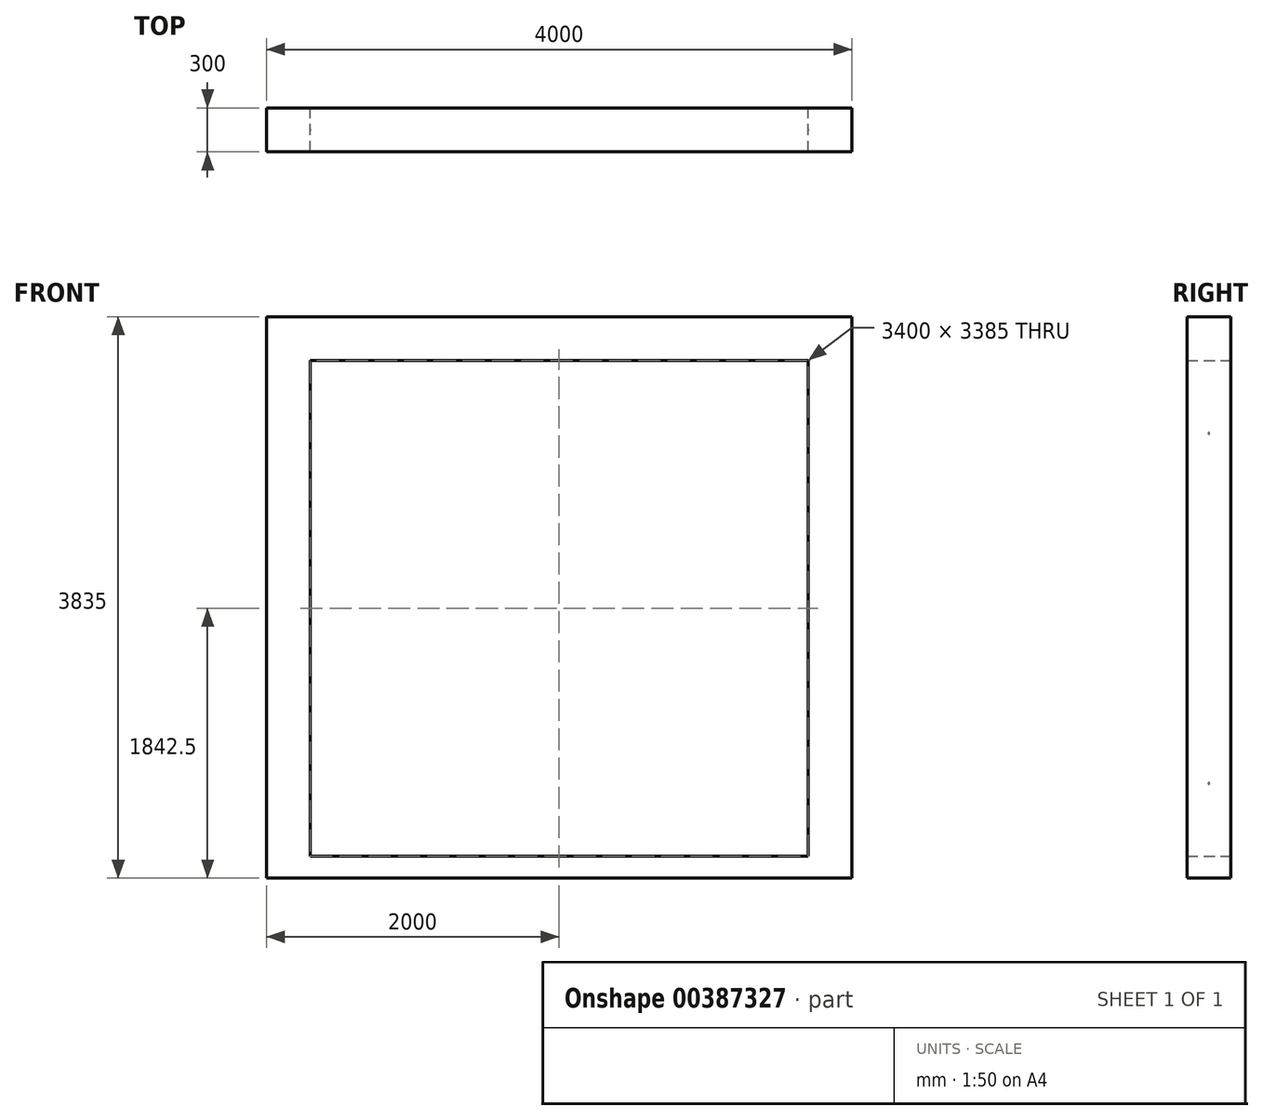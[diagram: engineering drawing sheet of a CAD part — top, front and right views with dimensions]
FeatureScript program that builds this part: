
annotation { "Feature Type Name" : "Feature", "Feature Type Description" : "" }
export const myFeature = defineFeature(function(context is Context, id is Id, definition is map)
    precondition{}
    {
        {
            var Q0;
            Q0=qCreatedBy(makeId("Front.planeOp"),FACE);
            var sketch = newSketch(context, id + "F0", { "sketchPlane" : qUnion([Q0])});
            skLineSegment(sketch, "E0.bottom", {"start": v(-3031.65, 3246.47) * mm, "end": v(368.35, 3246.47) * mm});
            skLineSegment(sketch, "E0.top", {"start": v(-3031.65, -138.53) * mm, "end": v(368.35, -138.53) * mm});
            skLineSegment(sketch, "E0.left", {"start": v(-3031.65, 3246.47) * mm, "end": v(-3031.65, -138.53) * mm});
            skLineSegment(sketch, "E0.right", {"start": v(368.35, 3246.47) * mm, "end": v(368.35, -138.53) * mm});
            skLineSegment(sketch, "E1.bottom", {"start": v(-3331.65, 3546.47) * mm, "end": v(668.35, 3546.47) * mm});
            skLineSegment(sketch, "E1.top", {"start": v(-3331.65, -138.53) * mm, "end": v(668.35, -138.53) * mm});
            skLineSegment(sketch, "E1.left", {"start": v(-3331.65, 3546.47) * mm, "end": v(-3331.65, -138.53) * mm});
            skLineSegment(sketch, "E1.right", {"start": v(668.35, 3546.47) * mm, "end": v(668.35, -138.53) * mm});
            skLineSegment(sketch, "E2", {"start": v(-1331.65, 3246.47) * mm, "end": v(-1331.65, -138.53) * mm, "construction": true});
            skLineSegment(sketch, "E3.top", {"start": v(-3331.65, -288.53) * mm, "end": v(668.35, -288.53) * mm});
            skLineSegment(sketch, "E3.left", {"start": v(-3331.65, -138.53) * mm, "end": v(-3331.65, -288.53) * mm});
            skLineSegment(sketch, "E3.right", {"start": v(668.35, -138.53) * mm, "end": v(668.35, -288.53) * mm});
            skSolve(sketch);
        }
        {
            var Q0;
            Q0=makeQuery(id+"F0.imprint","IMPRINT",FACE,{"disambiguationData":[TD([[makeQuery(id+"F0.imprint","IMPRINT",EDGE,{"derivedFrom":sQuery(id+"F0.wireOp",EDGE,"E0.bottom")}),1.0]])]});
            var Q1;
            Q1=makeQuery(id+"F0.imprint","IMPRINT",FACE,{"disambiguationData":[TD([[makeQuery(id+"F0.imprint","IMPRINT",EDGE,{"derivedFrom":sQuery(id+"F0.wireOp",EDGE,"E3.top")}),1.0]])]});
            extrude(context, id + "F1", {"entities" : qUnion([Q0, Q1]), "depth" : 300 * mm, "offsetDistance" : 25 * mm});
        }
        {
            var Q0;
            Q0=makeQuery(id+"F1.opExtrude","SWEPT_FACE",FACE,{"disambiguationData":[OSD([sQuery(id+"F0.wireOp",EDGE,"E0.left")])]});
            var sketch = newSketch(context, id + "F2", { "sketchPlane" : qUnion([Q0])});
            skPoint(sketch, "E4.positionSnap0", {"position": v(-150, -138.53) * mm});
            skLineSegment(sketch, "E5", {"start": v(0, 2748.97) * mm, "end": v(-300, 2748.97) * mm, "construction": true});
            skCircle(sketch, "E6", {"center": v(-150, 2748.97) * mm, "radius": 5 * mm});
            skLineSegment(sketch, "E7", {"start": v(0, 358.97) * mm, "end": v(-300, 358.97) * mm, "construction": true});
            skCircle(sketch, "E8", {"center": v(-150, 358.97) * mm, "radius": 5 * mm});
            skSolve(sketch);
        }
        {
            var Q0;
            Q0=makeQuery(id+"F2.imprint","IMPRINT",FACE,{"disambiguationData":[TD([[makeQuery(id+"F2.imprint","IMPRINT",EDGE,{"derivedFrom":sQuery(id+"F2.wireOp",EDGE,"E6")}),1.0]])]});
            var Q1;
            Q1=makeQuery(id+"F2.imprint","IMPRINT",FACE,{"disambiguationData":[TD([[makeQuery(id+"F2.imprint","IMPRINT",EDGE,{"derivedFrom":sQuery(id+"F2.wireOp",EDGE,"E8")}),1.0]])]});
            var Q2;
            Q2=sQuery(id+"F2.wireOp",EDGE,"E6");
            var Q3;
            Q3=sQuery(id+"F2.wireOp",EDGE,"E8");
            extrude(context, id + "F3", {"entities" : qUnion([Q0, Q1]), "surfaceEntities" : qUnion([Q2, Q3]), "depth" : 1 * mm, "offsetDistance" : 25 * mm});
        }
        {
            var Q0;
            Q0=makeQuery(id+"F1.opExtrude","SWEPT_FACE",FACE,{"disambiguationData":[OSD([sQuery(id+"F0.wireOp",EDGE,"E0.right")])]});
            var sketch = newSketch(context, id + "F4", { "sketchPlane" : qUnion([Q0])});
            skLineSegment(sketch, "E9", {"start": v(150, 3246.47) * mm, "end": v(150, 3246.47) * mm});
            skCircle(sketch, "E10", {"center": v(150, 2748.97) * mm, "radius": 5 * mm});
            skLineSegment(sketch, "E11", {"start": v(300, 358.97) * mm, "end": v(0, 358.97) * mm, "construction": true});
            skCircle(sketch, "E12", {"center": v(150, 358.97) * mm, "radius": 5 * mm});
            skSolve(sketch);
        }
        {
            var Q0;
            Q0=makeQuery(id+"F4.imprint","IMPRINT",FACE,{"disambiguationData":[TD([[makeQuery(id+"F4.imprint","IMPRINT",EDGE,{"derivedFrom":sQuery(id+"F4.wireOp",EDGE,"E10")}),1.0]])]});
            var Q1;
            Q1=makeQuery(id+"F4.imprint","IMPRINT",FACE,{"disambiguationData":[TD([[makeQuery(id+"F4.imprint","IMPRINT",EDGE,{"derivedFrom":sQuery(id+"F4.wireOp",EDGE,"E12")}),1.0]])]});
            extrude(context, id + "F5", {"entities" : qUnion([Q0, Q1]), "operationType" : NewBodyOperationType.ADD, "depth" : 1 * mm, "offsetDistance" : 25 * mm});
        }
    });
